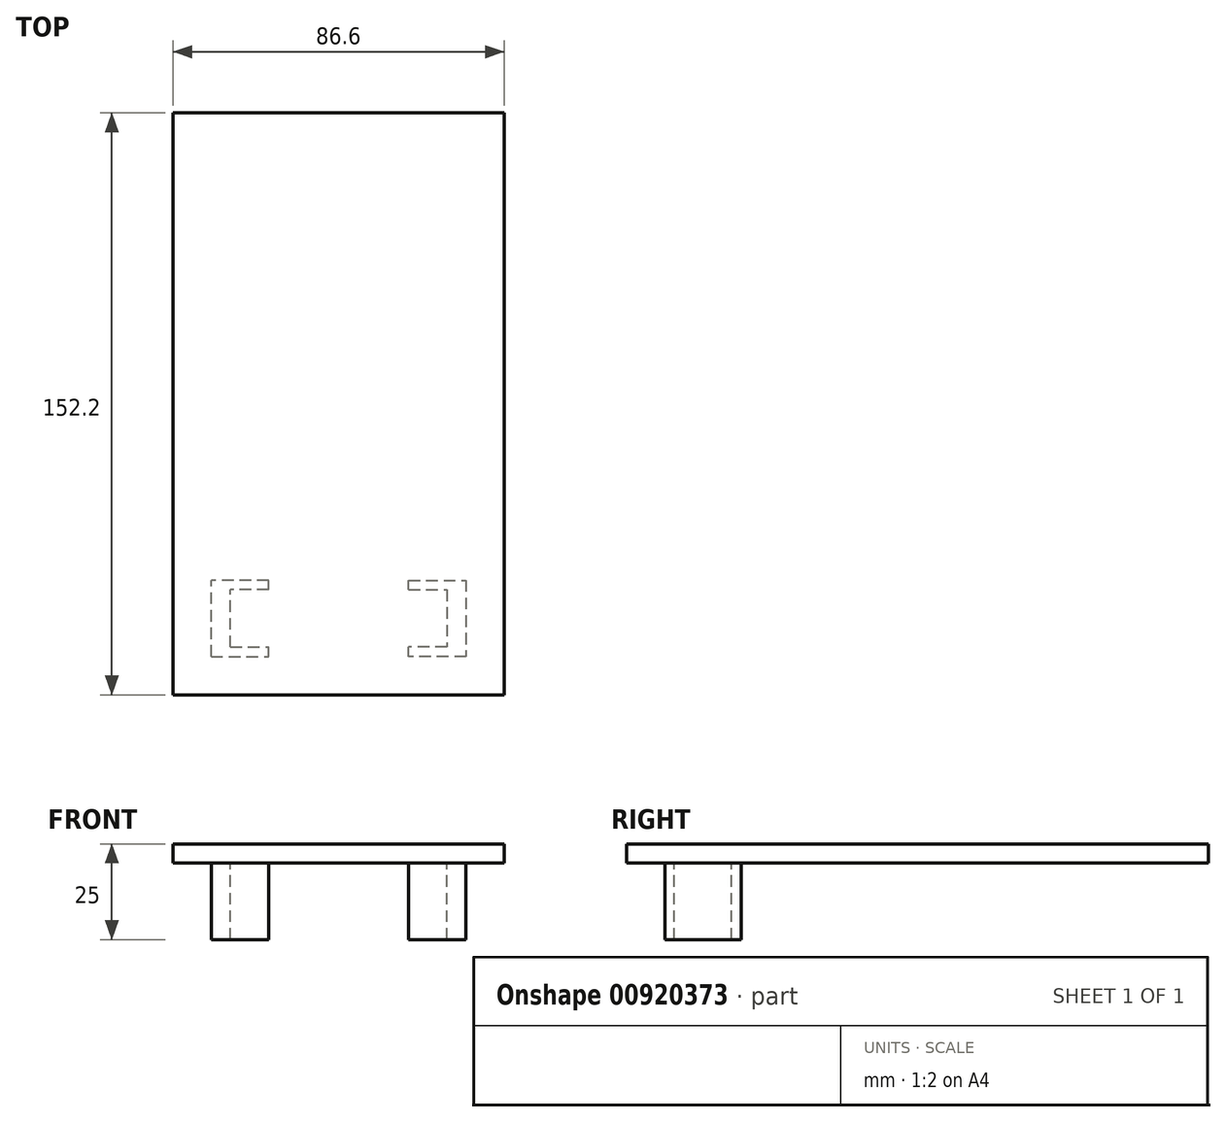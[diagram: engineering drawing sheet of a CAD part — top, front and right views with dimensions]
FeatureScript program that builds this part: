
annotation { "Feature Type Name" : "Feature", "Feature Type Description" : "" }
export const myFeature = defineFeature(function(context is Context, id is Id, definition is map)
    precondition{}
    {
        {
            var Q0;
            Q0=qCreatedBy(makeId("Top.planeOp"),FACE);
            var sketch = newSketch(context, id + "F0", { "sketchPlane" : qUnion([Q0])});
            skLineSegment(sketch, "E0.bottom", {"start": v(43.3, -76.1) * mm, "end": v(-43.3, -76.1) * mm});
            skLineSegment(sketch, "E0.top", {"start": v(43.3, 76.1) * mm, "end": v(-43.3, 76.1) * mm});
            skLineSegment(sketch, "E0.left", {"start": v(43.3, -76.1) * mm, "end": v(43.3, 76.1) * mm});
            skLineSegment(sketch, "E0.right", {"start": v(-43.3, -76.1) * mm, "end": v(-43.3, 76.1) * mm});
            skPoint(sketch, "E0.middle", {"position": v(0, 0) * mm});
            skSolve(sketch);
        }
        {
            var Q0;
            Q0 = qSketchRegion(id + "F0", true);
            extrude(context, id + "F1", {"entities" : qUnion([Q0]), "depth" : 5 * mm, "offsetDistance" : 25 * mm});
        }
        {
            var Q0;
            Q0=makeQuery(id+"F1.opExtrude","CAP_FACE",FACE,{"disambiguationData":[OSD([sQuery(id+"F0.wireOp",EDGE,"E0.bottom"),sQuery(id+"F0.wireOp",EDGE,"E0.top"),sQuery(id+"F0.wireOp",EDGE,"E0.left"),sQuery(id+"F0.wireOp",EDGE,"E0.right")])],"isStart":true});
            var sketch = newSketch(context, id + "F2", { "sketchPlane" : qUnion([Q0])});
            skLineSegment(sketch, "E1.bottom", {"start": v(-33.3, 66.1) * mm, "end": v(-28.3, 66.1) * mm});
            skLineSegment(sketch, "E1.top", {"start": v(-33.3, 46.1) * mm, "end": v(-28.3, 46.1) * mm});
            skLineSegment(sketch, "E1.left", {"start": v(-33.3, 66.1) * mm, "end": v(-33.3, 46.1) * mm});
            skLineSegment(sketch, "E1.right", {"start": v(-28.3, 66.1) * mm, "end": v(-28.3, 46.1) * mm});
            skLineSegment(sketch, "E2.bottom", {"start": v(28.3, 46.1) * mm, "end": v(33.3, 46.1) * mm});
            skLineSegment(sketch, "E2.top", {"start": v(28.3, 66.1) * mm, "end": v(33.3, 66.1) * mm});
            skLineSegment(sketch, "E2.left", {"start": v(28.3, 46.1) * mm, "end": v(28.3, 66.1) * mm});
            skLineSegment(sketch, "E2.right", {"start": v(33.3, 46.1) * mm, "end": v(33.3, 66.1) * mm});
            skLineSegment(sketch, "E3.bottom", {"start": v(18.3, 48.6) * mm, "end": v(28.3, 48.6) * mm});
            skLineSegment(sketch, "E3.top", {"start": v(18.3, 46.1) * mm, "end": v(28.3, 46.1) * mm});
            skLineSegment(sketch, "E3.left", {"start": v(18.3, 48.6) * mm, "end": v(18.3, 46.1) * mm});
            skLineSegment(sketch, "E3.right", {"start": v(28.3, 48.6) * mm, "end": v(28.3, 46.1) * mm});
            skLineSegment(sketch, "E4.bottom", {"start": v(-18.3, 48.6) * mm, "end": v(-28.3, 48.6) * mm});
            skLineSegment(sketch, "E4.top", {"start": v(-18.3, 46.1) * mm, "end": v(-28.3, 46.1) * mm});
            skLineSegment(sketch, "E4.left", {"start": v(-18.3, 48.6) * mm, "end": v(-18.3, 46.1) * mm});
            skLineSegment(sketch, "E4.right", {"start": v(-28.3, 48.6) * mm, "end": v(-28.3, 46.1) * mm});
            skLineSegment(sketch, "E5.bottom", {"start": v(-28.3, 66.1) * mm, "end": v(-18.3, 66.1) * mm});
            skLineSegment(sketch, "E5.top", {"start": v(-28.3, 63.6) * mm, "end": v(-18.3, 63.6) * mm});
            skLineSegment(sketch, "E5.left", {"start": v(-28.3, 66.1) * mm, "end": v(-28.3, 63.6) * mm});
            skLineSegment(sketch, "E5.right", {"start": v(-18.3, 66.1) * mm, "end": v(-18.3, 63.6) * mm});
            skLineSegment(sketch, "E6.bottom", {"start": v(28.3, 66.1) * mm, "end": v(18.3, 66.1) * mm});
            skLineSegment(sketch, "E6.top", {"start": v(28.3, 63.6) * mm, "end": v(18.3, 63.6) * mm});
            skLineSegment(sketch, "E6.left", {"start": v(28.3, 66.1) * mm, "end": v(28.3, 63.6) * mm});
            skLineSegment(sketch, "E6.right", {"start": v(18.3, 66.1) * mm, "end": v(18.3, 63.6) * mm});
            skSolve(sketch);
        }
        {
            var Q0;
            Q0 = qSketchRegion(id + "F2", true);
            extrude(context, id + "F3", {"entities" : qUnion([Q0]), "operationType" : NewBodyOperationType.ADD, "depth" : 20 * mm, "offsetDistance" : 25 * mm});
        }
    });
